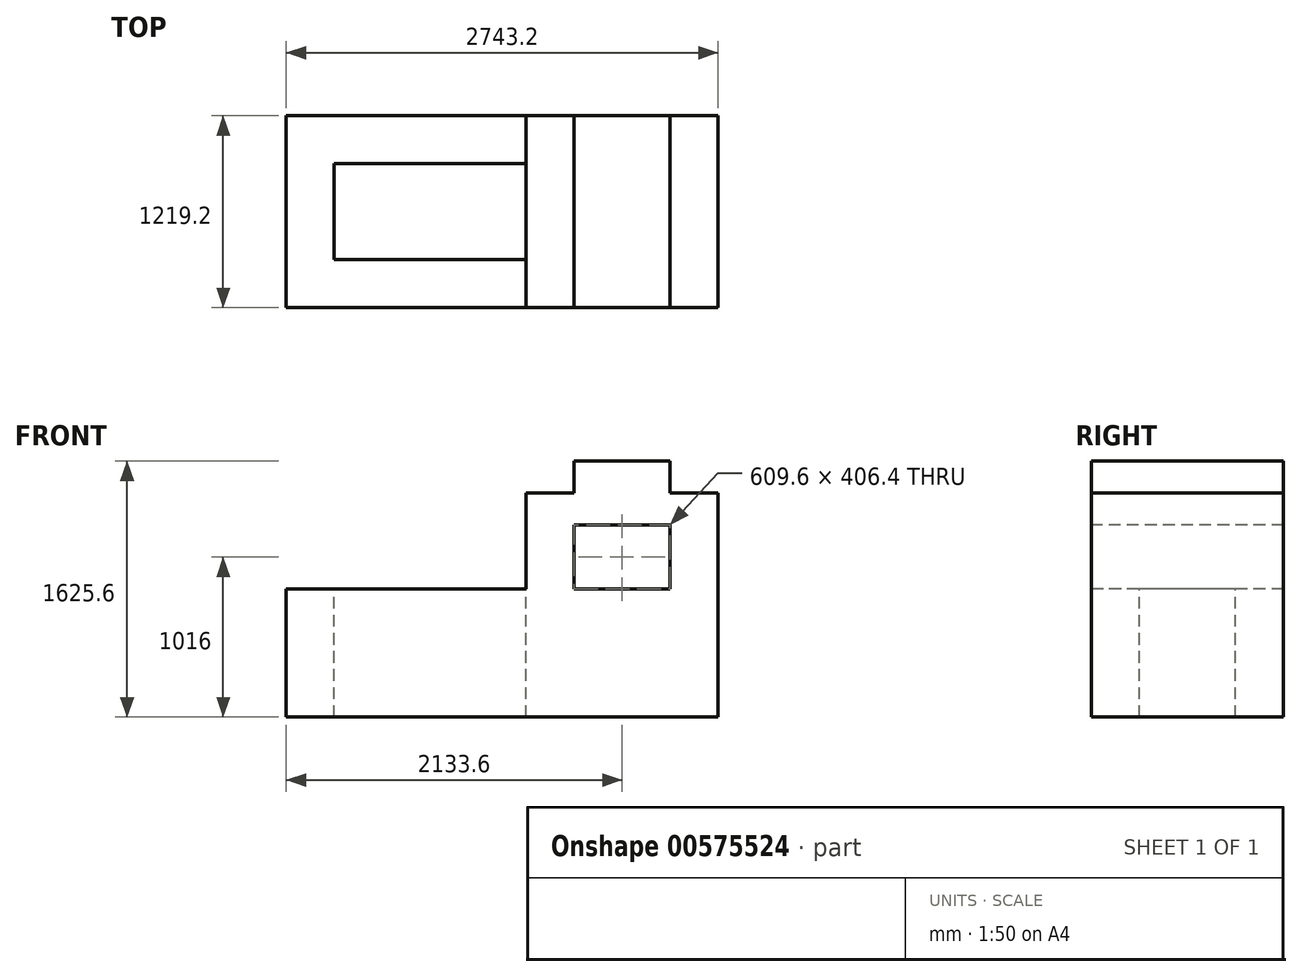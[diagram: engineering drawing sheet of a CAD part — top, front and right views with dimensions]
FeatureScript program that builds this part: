
annotation { "Feature Type Name" : "Feature", "Feature Type Description" : "" }
export const myFeature = defineFeature(function(context is Context, id is Id, definition is map)
    precondition{}
    {
        {
            var Q0;
            Q0=qCreatedBy(makeId("Front.planeOp"),FACE);
            var sketch = newSketch(context, id + "F0", { "sketchPlane" : qUnion([Q0])});
            skLineSegment(sketch, "E0.bottom", {"start": v(-2690.27, 1587.64) * mm, "end": v(52.93, 1587.64) * mm});
            skLineSegment(sketch, "E0.top", {"start": v(-2690.27, -37.96) * mm, "end": v(52.93, -37.96) * mm});
            skLineSegment(sketch, "E0.left", {"start": v(-2690.27, 1587.64) * mm, "end": v(-2690.27, -37.96) * mm});
            skLineSegment(sketch, "E0.right", {"start": v(52.93, 1587.64) * mm, "end": v(52.93, -37.96) * mm});
            skSolve(sketch);
        }
        {
            var Q0;
            Q0=makeQuery(id+"F0.imprint","IMPRINT",FACE,{"disambiguationData":[TD([[makeQuery(id+"F0.imprint","IMPRINT",EDGE,{"derivedFrom":sQuery(id+"F0.wireOp",EDGE,"E0.bottom")}),-1.0]])]});
            extrude(context, id + "F1", {"entities" : qUnion([Q0]), "depth" : 1219.2 * mm, "offsetDistance" : 25.4 * mm});
        }
        {
            var Q0;
            Q0=makeQuery(id+"F1.opExtrude","CAP_FACE",FACE,{"disambiguationData":[OSD([sQuery(id+"F0.wireOp",EDGE,"E0.bottom"),sQuery(id+"F0.wireOp",EDGE,"E0.top"),sQuery(id+"F0.wireOp",EDGE,"E0.left"),sQuery(id+"F0.wireOp",EDGE,"E0.right")])],"isStart":false});
            var sketch = newSketch(context, id + "F2", { "sketchPlane" : qUnion([Q0])});
            skLineSegment(sketch, "E1.bottom", {"start": v(52.93, 1587.64) * mm, "end": v(-251.87, 1587.64) * mm});
            skLineSegment(sketch, "E1.top", {"start": v(52.93, 1384.44) * mm, "end": v(-251.87, 1384.44) * mm});
            skLineSegment(sketch, "E1.left", {"start": v(52.93, 1587.64) * mm, "end": v(52.93, 1384.44) * mm});
            skLineSegment(sketch, "E1.right", {"start": v(-251.87, 1587.64) * mm, "end": v(-251.87, 1384.44) * mm});
            skSolve(sketch);
        }
        {
            var Q0;
            Q0=makeQuery(id+"F2.imprint","IMPRINT",FACE,{"disambiguationData":[TD([[makeQuery(id+"F2.imprint","IMPRINT",EDGE,{"derivedFrom":sQuery(id+"F2.wireOp",EDGE,"E1.bottom")}),-1.0]])]});
            extrude(context, id + "F3", {"entities" : qUnion([Q0]), "operationType" : NewBodyOperationType.REMOVE, "endBound" : BoundingType.THROUGH_ALL, "oppositeDirection" : true, "depth" : 25.4 * mm, "offsetDistance" : 25.4 * mm});
        }
        {
            var Q0;
            Q0=makeQuery(id+"F1.opExtrude","CAP_FACE",FACE,{"disambiguationData":[OSD([sQuery(id+"F0.wireOp",EDGE,"E0.bottom"),sQuery(id+"F0.wireOp",EDGE,"E0.top"),sQuery(id+"F0.wireOp",EDGE,"E0.left"),sQuery(id+"F0.wireOp",EDGE,"E0.right")])],"isStart":false});
            var sketch = newSketch(context, id + "F4", { "sketchPlane" : qUnion([Q0])});
            skLineSegment(sketch, "E2.bottom", {"start": v(-2690.27, 1587.64) * mm, "end": v(-1166.27, 1587.64) * mm});
            skLineSegment(sketch, "E2.top", {"start": v(-2690.27, 774.84) * mm, "end": v(-1166.27, 774.84) * mm});
            skLineSegment(sketch, "E2.left", {"start": v(-2690.27, 1587.64) * mm, "end": v(-2690.27, 774.84) * mm});
            skLineSegment(sketch, "E2.right", {"start": v(-1166.27, 1587.64) * mm, "end": v(-1166.27, 774.84) * mm});
            skSolve(sketch);
        }
        {
            var Q0;
            Q0=makeQuery(id+"F4.imprint","IMPRINT",FACE,{"disambiguationData":[TD([[makeQuery(id+"F4.imprint","IMPRINT",EDGE,{"derivedFrom":sQuery(id+"F4.wireOp",EDGE,"E2.bottom")}),-1.0]])]});
            extrude(context, id + "F5", {"entities" : qUnion([Q0]), "operationType" : NewBodyOperationType.REMOVE, "endBound" : BoundingType.THROUGH_ALL, "oppositeDirection" : true, "depth" : 25.4 * mm, "offsetDistance" : 25.4 * mm});
        }
        {
            var Q0;
            Q0=makeQuery(id+"F1.opExtrude","CAP_FACE",FACE,{"disambiguationData":[OSD([sQuery(id+"F0.wireOp",EDGE,"E0.bottom"),sQuery(id+"F0.wireOp",EDGE,"E0.top"),sQuery(id+"F0.wireOp",EDGE,"E0.left"),sQuery(id+"F0.wireOp",EDGE,"E0.right")])],"isStart":false});
            var sketch = newSketch(context, id + "F6", { "sketchPlane" : qUnion([Q0])});
            skLineSegment(sketch, "E3.bottom", {"start": v(-1166.27, 1587.64) * mm, "end": v(-861.47, 1587.64) * mm});
            skLineSegment(sketch, "E3.top", {"start": v(-1166.27, 1384.44) * mm, "end": v(-861.47, 1384.44) * mm});
            skLineSegment(sketch, "E3.left", {"start": v(-1166.27, 1587.64) * mm, "end": v(-1166.27, 1384.44) * mm});
            skLineSegment(sketch, "E3.right", {"start": v(-861.47, 1587.64) * mm, "end": v(-861.47, 1384.44) * mm});
            skSolve(sketch);
        }
        {
            var Q0;
            Q0=makeQuery(id+"F6.imprint","IMPRINT",FACE,{"disambiguationData":[TD([[makeQuery(id+"F6.imprint","IMPRINT",EDGE,{"derivedFrom":sQuery(id+"F6.wireOp",EDGE,"E3.bottom")}),-1.0]])]});
            extrude(context, id + "F7", {"entities" : qUnion([Q0]), "operationType" : NewBodyOperationType.ADD, "endBound" : BoundingType.THROUGH_ALL, "depth" : 25.4 * mm, "offsetDistance" : 25.4 * mm});
        }
        {
            var Q0;
            Q0=makeQuery(id+"F7.opExtrude","CAP_FACE",FACE,{"disambiguationData":[OSD([sQuery(id+"F6.wireOp",EDGE,"E3.bottom"),sQuery(id+"F6.wireOp",EDGE,"E3.top"),sQuery(id+"F6.wireOp",EDGE,"E3.left"),sQuery(id+"F6.wireOp",EDGE,"E3.right")])],"isStart":false});
            extrude(context, id + "F8", {"entities" : qUnion([Q0]), "operationType" : NewBodyOperationType.REMOVE, "endBound" : BoundingType.THROUGH_ALL, "oppositeDirection" : true, "depth" : 25.4 * mm, "offsetDistance" : 25.4 * mm});
        }
        {
            var Q0;
            Q0=makeQuery(id+"F1.opExtrude","CAP_FACE",FACE,{"disambiguationData":[OSD([sQuery(id+"F0.wireOp",EDGE,"E0.bottom"),sQuery(id+"F0.wireOp",EDGE,"E0.top"),sQuery(id+"F0.wireOp",EDGE,"E0.left"),sQuery(id+"F0.wireOp",EDGE,"E0.right")])],"isStart":false});
            var sketch = newSketch(context, id + "F9", { "sketchPlane" : qUnion([Q0])});
            skLineSegment(sketch, "E4.bottom", {"start": v(-861.47, 1181.24) * mm, "end": v(-251.87, 1181.24) * mm});
            skLineSegment(sketch, "E4.top", {"start": v(-861.47, 774.84) * mm, "end": v(-251.87, 774.84) * mm});
            skLineSegment(sketch, "E4.left", {"start": v(-861.47, 1181.24) * mm, "end": v(-861.47, 774.84) * mm});
            skLineSegment(sketch, "E4.right", {"start": v(-251.87, 1181.24) * mm, "end": v(-251.87, 774.84) * mm});
            skSolve(sketch);
        }
        {
            var Q0;
            Q0=makeQuery(id+"F9.imprint","IMPRINT",FACE,{"disambiguationData":[TD([[makeQuery(id+"F9.imprint","IMPRINT",EDGE,{"derivedFrom":sQuery(id+"F9.wireOp",EDGE,"E4.bottom")}),-1.0]])]});
            extrude(context, id + "F10", {"entities" : qUnion([Q0]), "operationType" : NewBodyOperationType.REMOVE, "endBound" : BoundingType.THROUGH_ALL, "oppositeDirection" : true, "depth" : 25.4 * mm, "offsetDistance" : 25.4 * mm});
        }
        {
            var Q0;
            Q0=makeQuery(id+"F5.boolean.opBoolean","COPY",FACE,{"derivedFrom":makeQuery(id+"F5.opExtrude","SWEPT_FACE",FACE,{"disambiguationData":[OSD([sQuery(id+"F4.wireOp",EDGE,"E2.top")])]})});
            var sketch = newSketch(context, id + "F11", { "sketchPlane" : qUnion([Q0])});
            skLineSegment(sketch, "E5.bottom", {"start": v(-2385.47, -304.8) * mm, "end": v(-1166.27, -304.8) * mm});
            skLineSegment(sketch, "E5.top", {"start": v(-2385.47, -914.4) * mm, "end": v(-1166.27, -914.4) * mm});
            skLineSegment(sketch, "E5.left", {"start": v(-2385.47, -304.8) * mm, "end": v(-2385.47, -914.4) * mm});
            skLineSegment(sketch, "E5.right", {"start": v(-1166.27, -304.8) * mm, "end": v(-1166.27, -914.4) * mm});
            skSolve(sketch);
        }
        {
            var Q0;
            Q0=makeQuery(id+"F11.imprint","IMPRINT",FACE,{"disambiguationData":[TD([[makeQuery(id+"F11.imprint","IMPRINT",EDGE,{"derivedFrom":sQuery(id+"F11.wireOp",EDGE,"E5.bottom")}),-1.0]])]});
            extrude(context, id + "F12", {"entities" : qUnion([Q0]), "operationType" : NewBodyOperationType.REMOVE, "endBound" : BoundingType.THROUGH_ALL, "oppositeDirection" : true, "depth" : 25.4 * mm, "offsetDistance" : 25.4 * mm});
        }
    });
